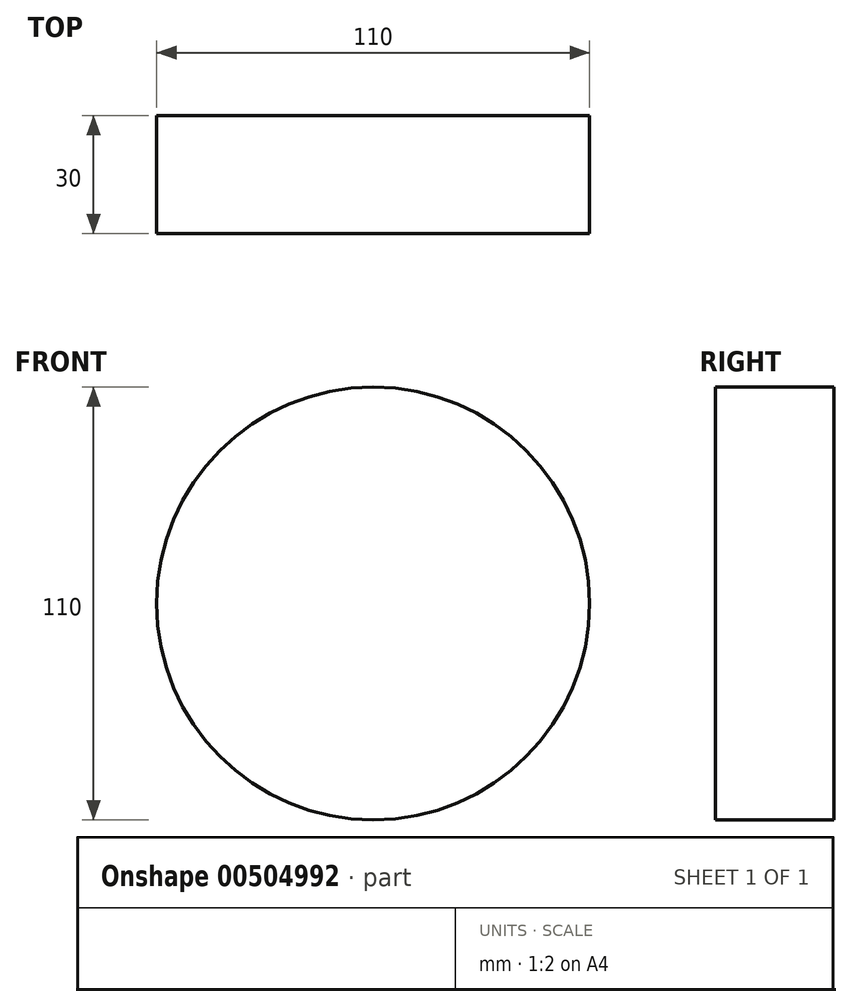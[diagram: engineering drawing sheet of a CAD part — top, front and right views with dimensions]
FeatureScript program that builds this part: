
annotation { "Feature Type Name" : "Feature", "Feature Type Description" : "" }
export const myFeature = defineFeature(function(context is Context, id is Id, definition is map)
    precondition{}
    {
        {
            var Q0;
            Q0=qCreatedBy(makeId("Front.planeOp"),FACE);
            var sketch = newSketch(context, id + "F0", { "sketchPlane" : qUnion([Q0])});
            skCircle(sketch, "E0", {"center": v(0, 0) * mm, "radius": 55 * mm});
            skCircle(sketch, "E1.0", {"center": v(0, 0) * mm, "radius": 60 * mm});
            skSolve(sketch);
        }
        {
            var Q0;
            Q0 = qSketchRegion(id + "F0", true);
            var Q1;
            Q1=sQuery(id+"F0.wireOp",EDGE,"E0");
            extrude(context, id + "F1", {"entities" : qUnion([Q0]), "bodyType" : ToolBodyType.SURFACE, "surfaceEntities" : qUnion([Q1]), "depth" : 30 * mm, "offsetDistance" : 25 * mm});
        }
    });
